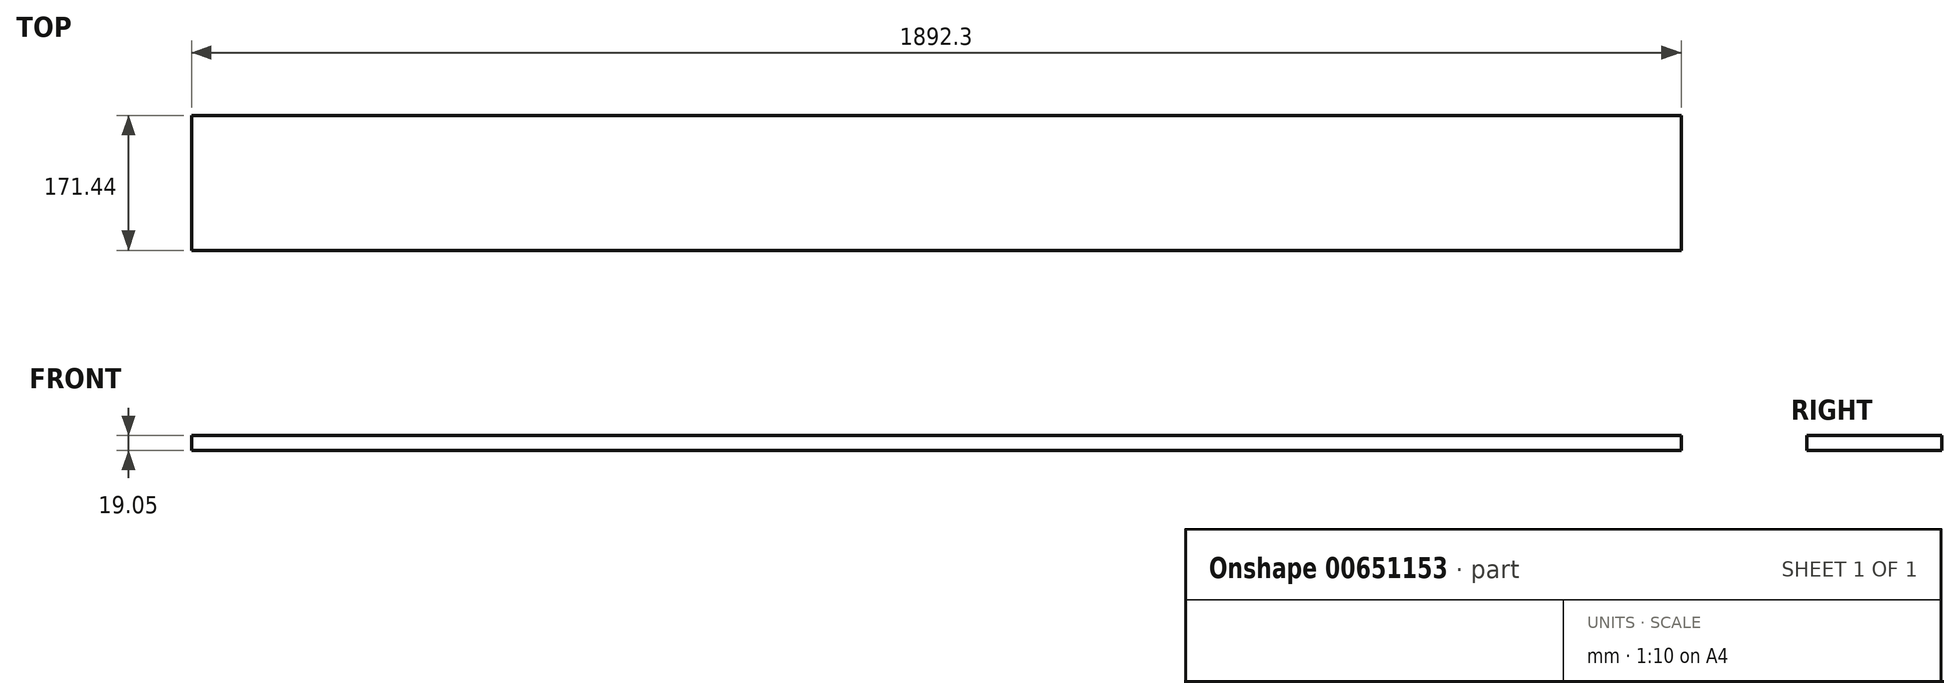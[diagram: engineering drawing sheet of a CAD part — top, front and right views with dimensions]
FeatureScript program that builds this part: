
annotation { "Feature Type Name" : "Feature", "Feature Type Description" : "" }
export const myFeature = defineFeature(function(context is Context, id is Id, definition is map)
    precondition{}
    {
        {
            var Q0;
            Q0=qCreatedBy(makeId("Top.planeOp"),FACE);
            var sketch = newSketch(context, id + "F0", { "sketchPlane" : qUnion([Q0])});
            skLineSegment(sketch, "E0.bottom", {"start": v(946.15, 85.72) * mm, "end": v(-946.15, 85.72) * mm});
            skLineSegment(sketch, "E0.top", {"start": v(946.15, -85.73) * mm, "end": v(-946.15, -85.73) * mm});
            skLineSegment(sketch, "E0.left", {"start": v(946.15, 85.72) * mm, "end": v(946.15, -85.73) * mm});
            skLineSegment(sketch, "E0.right", {"start": v(-946.15, 85.72) * mm, "end": v(-946.15, -85.73) * mm});
            skPoint(sketch, "E0.middle", {"position": v(0, 0) * mm});
            skSolve(sketch);
        }
        {
            var Q0;
            Q0=makeQuery(id+"F0.imprint","IMPRINT",FACE,{"disambiguationData":[TD([[makeQuery(id+"F0.imprint","IMPRINT",EDGE,{"derivedFrom":sQuery(id+"F0.wireOp",EDGE,"E0.bottom")}),1.0]])]});
            extrude(context, id + "F1", {"entities" : qUnion([Q0]), "depth" : 19.05 * mm, "offsetDistance" : 25.4 * mm});
        }
    });
